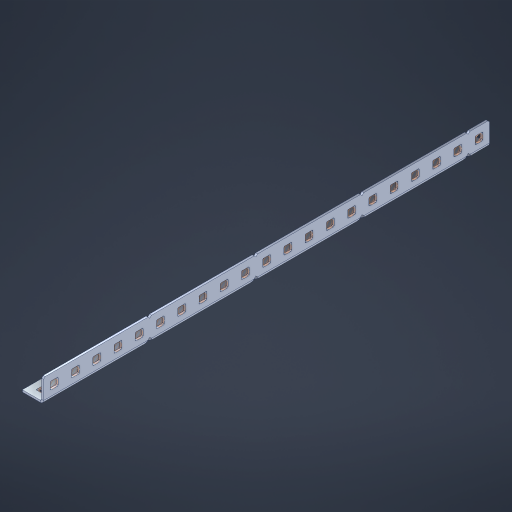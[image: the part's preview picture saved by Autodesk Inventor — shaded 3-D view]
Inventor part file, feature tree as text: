
AUTODESK INVENTOR PART (.ipt)
format: ipt  version: 2023 (Build 270158000, 158)  size: 775,168 bytes
history: native  units: in
note: dims shown in document units (in); Inventor stores cm internally (conversion verified against a paired STEP export)
features: other x47, extrude x41, sheet_metal_op x10, sketch x8, mirror x1, pattern_linear x1, chamfer x1
ambient origin geometry x8: Origin, YZ Plane, XZ Plane, XY Plane, X Axis, Y Axis, Z Axis, Center Point
bodies: Solid1 (feature_tree), Body (feature_tree)
feature tree (109):
  other  "Flange Pattern Plane"
  sheet_metal_op  "Flange Pattern"
  sheet_metal_op  "Body Pattern"
  other  "Arc Length"
  mirror  "Notch Mirror"
  pattern_linear  "Notch Pattern"  Spacing1=0.1875in  [1 undecoded]
  chamfer  "End Chamfer"
  extrude  "Half Cut"  Depth=0.0469in
  sketch  "Sketch1"  dims[d0=2.5in]
  other  "Plate1"
  sketch  "Sketch2"  dims[d1=10.5in]
  other  "Plate2"
  sheet_metal_op  "Bend1"
  sheet_metal_op  "Corner1"
  sketch  "Sketch3"  dims[d2=0.0469in]
  other  "Flange Pattern Sketch"
  sketch  "Sketch7"  dims[d3=0.0469in]
  other  "Srf1"
  other  "Srf2"
  sketch  "Sketch8"  dims[d4=0.0234in]
  sketch  "Sketch9"  dims[d5=0.0938in]
  other  "Srf91"
  sheet_metal_op  "Body Pattern Sketch"
  other  "Srf92"
  sketch  "Sketch13"  dims[d6=0.0469in]
  sketch  "Sketch14"  dims[d7=0.5in d8=90.0deg d9=0.0312in d10=0.1875in d11=0.0469in d12=0.0469in d16=0.182in d17=0.02in d18=0.0469in d19=0.0in d20=0.25in d21=0.25in d46=0.172in d47=1.0in d48=0.0in d49=0.182in d50=0.02in d51=0.25in d52=0.25in d53=0.0469in d54=0.0in d55=0.172in d56=1.0in d57=0.0in d60=8.2677in d62=0.5in d63=0.3937in d65=0.5in d85=0.1227in d86=0.1659in d88=0.04in d89=0.0469in d90=0.0in d91=0.04in d92=0.0491in d95=2.5in d96=0.04in d97=0.25in d98=45.0deg d101=0.0in d102=2.497in d131=0.5in d132=8.2677in d134=0.5in d139=0.5in]
  other  "Srf856"
  other  "Srf1310"
  other  "Srf1311"
  other  "Srf1312"
  other  "Srf1376"
  other  "Srf1377"
  other  "Srf1728"
  other  "Srf1755"
  other  "Srf1878"
  other  "Srf1879"
  other  "Srf1880"
  other  "Srf1881"
  other  "Srf1882"
  other  "Srf1883"
  other  "Srf1884"
  other  "Srf1885"
  other  "Srf1886"
  other  "Srf1887"
  other  "Srf1888"
  other  "Srf1889"
  other  "Srf1890"
  other  "Srf1891"
  other  "Srf1892"
  other  "Srf1942"
  other  "Srf1943"
  other  "Srf1944"
  other  "Srf1945"
  other  "Srf1946"
  other  "Srf1947"
  other  "Srf1948"
  other  "Srf1949"
  other  "Srf1950"
  other  "Srf1951"
  other  "Srf1952"
  other  "Srf1953"
  other  "Srf1954"
  other  "Srf1955"
  other  "Srf1956"
  sheet_metal_op  "Flange Stamp"
  sheet_metal_op  "Flange Circle"
  sheet_metal_op  "Body Stamp"
  sheet_metal_op  "Body Circle"
  sheet_metal_op  "Notch"
  extrude  "ExtrusionSrf2"  Depth=0.0469in
  extrude  "ExtrusionSrf92"  Depth=0.5in
  extrude  "ExtrusionSrf856"  Depth=0.02in
  extrude  "ExtrusionSrf1310"  Depth=0.0469in
  extrude  "ExtrusionSrf1311"  TaperAngle=0.0deg  [1 undecoded]
  extrude  "ExtrusionSrf1312"  Depth=0.5in
  extrude  "ExtrusionSrf1376"  Depth=0.5in
  extrude  "ExtrusionSrf1377"  Depth=0.5in
  extrude  "ExtrusionSrf1728"  Depth=0.5in TaperAngle=0.0deg
  extrude  "ExtrusionSrf1755"  Depth=0.5in
  extrude  "ExtrusionSrf1878"  Depth=0.02in
  extrude  "ExtrusionSrf1879"  Depth=0.5in
  extrude  "ExtrusionSrf1880"  Depth=0.5in
  extrude  "ExtrusionSrf1881"  Depth=0.0469in
  extrude  "ExtrusionSrf1882"  TaperAngle=0.0deg  [1 undecoded]
  extrude  "ExtrusionSrf1883"  Depth=0.5in
  extrude  "ExtrusionSrf1884"  Depth=0.5in TaperAngle=0.0deg
  extrude  "ExtrusionSrf1885"  Depth=0.5in
  extrude  "ExtrusionSrf1886"  Depth=0.5in
  extrude  "ExtrusionSrf1887"  Depth=0.5in
  extrude  "ExtrusionSrf1888"  Depth=0.5in
  extrude  "ExtrusionSrf1889"  Depth=0.5in
  extrude  "ExtrusionSrf1890"  Depth=0.0469in
  extrude  "ExtrusionSrf1891"  TaperAngle=0.0deg  [1 undecoded]
  extrude  "ExtrusionSrf1892"  Depth=0.5in
  extrude  "ExtrusionSrf1942"  Depth=0.5in
  extrude  "ExtrusionSrf1943"  Depth=0.5in
  extrude  "ExtrusionSrf1944"  Depth=0.5in TaperAngle=45.0deg
  extrude  "ExtrusionSrf1945"  TaperAngle=0.0deg  [1 undecoded]
  extrude  "ExtrusionSrf1946"  Depth=0.5in
  extrude  "ExtrusionSrf1947"  Depth=0.5in
  extrude  "ExtrusionSrf1948"  Depth=0.5in
  extrude  "ExtrusionSrf1949"  Depth=0.5in
  extrude  "ExtrusionSrf1950"  Depth=0.5in
  extrude  "ExtrusionSrf1951"  [1 undecoded]
  extrude  "ExtrusionSrf1952"  [1 undecoded]
  extrude  "ExtrusionSrf1953"  [1 undecoded]
  extrude  "ExtrusionSrf1954"  [1 undecoded]
  extrude  "ExtrusionSrf1955"  [1 undecoded]
  extrude  "ExtrusionSrf1956"  [1 undecoded]
note: 11 required parameter values undecoded (feature->parameter linkage not recoverable at this tier; creation-order binding heuristic only, values carry confidence <= 0.55)
